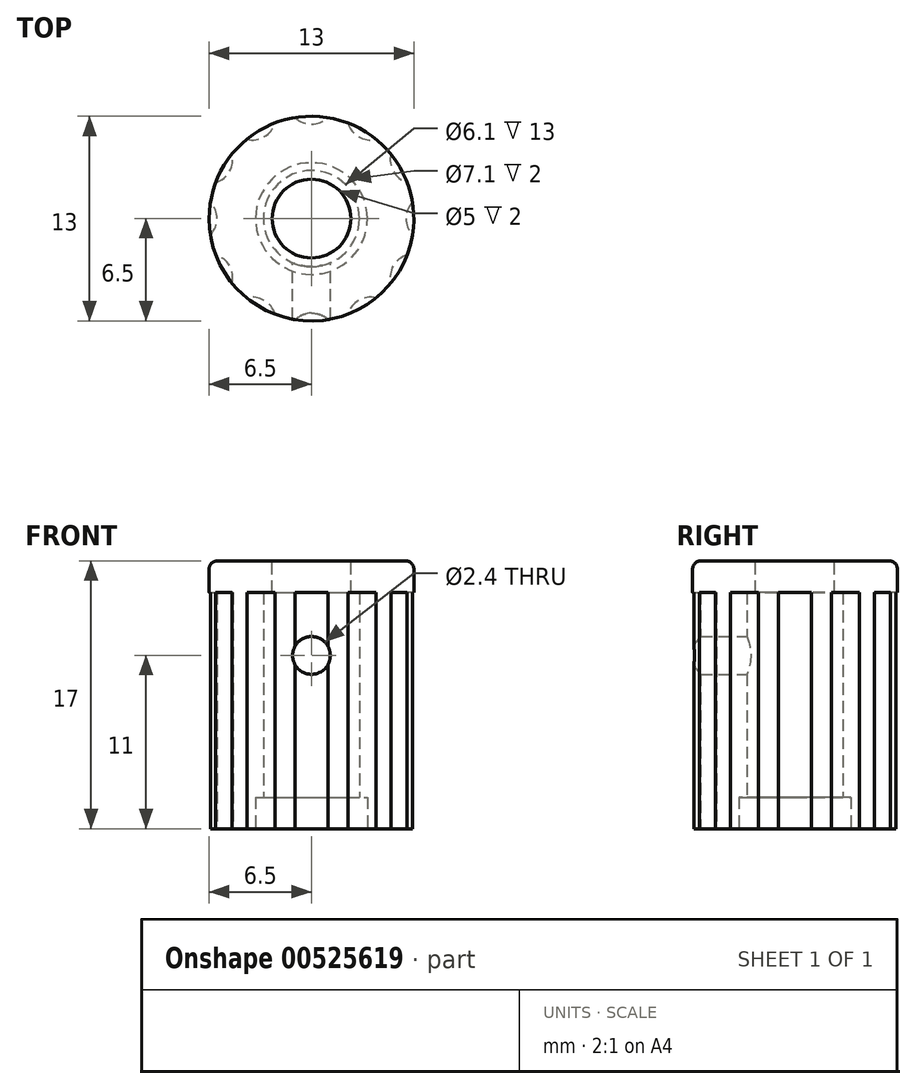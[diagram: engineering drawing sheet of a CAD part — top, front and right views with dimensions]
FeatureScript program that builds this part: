
annotation { "Feature Type Name" : "Feature", "Feature Type Description" : "" }
export const myFeature = defineFeature(function(context is Context, id is Id, definition is map)
    precondition{}
    {
        {
            var Q0;
            Q0=qCreatedBy(makeId("Front.planeOp"),FACE);
            var sketch = newSketch(context, id + "F0", { "sketchPlane" : qUnion([Q0])});
            skLineSegment(sketch, "E0", {"start": v(0, -2.23) * mm, "end": v(0, -5.1) * mm, "construction": true});
            skLineSegment(sketch, "E1", {"start": v(0, 0) * mm, "end": v(-5, 0) * mm});
            skLineSegment(sketch, "E2", {"start": v(-5, 0) * mm, "end": v(-5, 0) * mm});
            skLineSegment(sketch, "E3", {"start": v(-5, 0) * mm, "end": v(-6.5, 0) * mm});
            skLineSegment(sketch, "E4", {"start": v(-6.5, 0) * mm, "end": v(-6.5, 17) * mm});
            skLineSegment(sketch, "E5", {"start": v(-6.5, 17) * mm, "end": v(0, 17) * mm});
            skLineSegment(sketch, "E6", {"start": v(0, 0) * mm, "end": v(0, 17) * mm});
            skSolve(sketch);
        }
        {
            var Q0;
            Q0=qSketchRegion(id+"F0",true);
            var Q1;
            Q1=sQuery(id+"F0.wireOp",EDGE,"E0");
            revolve(context, id + "F1", {"entities" : qUnion([Q0]), "axis" : qUnion([Q1]), "revolveType" : RevolveType.FULL});
        }
        {
            var Q0;
            Q0=makeQuery(id+"F1.opRevolve","SWEPT_FACE",FACE,{"disambiguationData":[OSD([sQuery(id+"F0.wireOp",EDGE,"E1")])]});
            var sketch = newSketch(context, id + "F2", { "sketchPlane" : qUnion([Q0])});
            skCircle(sketch, "E7", {"center": v(0, 0) * mm, "radius": 3.05 * mm});
            skSolve(sketch);
        }
        {
            var Q0;
            Q0=qSketchRegion(id+"F2",true);
            extrude(context, id + "F3", {"entities" : qUnion([Q0]), "operationType" : NewBodyOperationType.REMOVE, "oppositeDirection" : true, "depth" : 15 * mm, "offsetDistance" : 25 * mm});
        }
        {
            var Q0;
            Q0=makeQuery(id+"F1.opRevolve","SWEPT_EDGE",EDGE,{"disambiguationData":[OSD([sQuery(id+"F0.wireOp",EDGE,"E4"),sQuery(id+"F0.wireOp",EDGE,"E5")])]});
            fillet(context, id + "F4", {"entities" : qUnion([Q0]), "radius" : 0.5 * mm, "tangentPropagation" : true, "allowEdgeOverflow" : false});
        }
        {
            var Q0;
            Q0=qCreatedBy(makeId("Front.planeOp"),FACE);
            var sketch = newSketch(context, id + "F5", { "sketchPlane" : qUnion([Q0])});
            skCircle(sketch, "E8", {"center": v(0, 11) * mm, "radius": 1.2 * mm});
            skSolve(sketch);
        }
        {
            var Q0;
            Q0=qSketchRegion(id+"F5",true);
            extrude(context, id + "F6", {"entities" : qUnion([Q0]), "operationType" : NewBodyOperationType.REMOVE, "depth" : 7 * mm, "offsetDistance" : 25 * mm});
        }
        {
            var Q0;
            Q0=makeQuery(id+"F1.opRevolve","SWEPT_FACE",FACE,{"disambiguationData":[OSD([sQuery(id+"F0.wireOp",EDGE,"E3")])]});
            var sketch = newSketch(context, id + "F7", { "sketchPlane" : qUnion([Q0])});
            skCircle(sketch, "E9", {"center": v(-7.5, 0) * mm, "radius": 1.5 * mm});
            skCircle(sketch, "E10.1.0", {"center": v(-6.5, -3.75) * mm, "radius": 1.5 * mm});
            skCircle(sketch, "E10.2.0", {"center": v(-3.75, -6.5) * mm, "radius": 1.5 * mm});
            skCircle(sketch, "E10.3.0", {"center": v(0, -7.5) * mm, "radius": 1.5 * mm});
            skCircle(sketch, "E10.4.0", {"center": v(3.75, -6.5) * mm, "radius": 1.5 * mm});
            skCircle(sketch, "E10.5.0", {"center": v(6.5, -3.75) * mm, "radius": 1.5 * mm});
            skCircle(sketch, "E10.6.0", {"center": v(7.5, 0) * mm, "radius": 1.5 * mm});
            skCircle(sketch, "E10.7.0", {"center": v(6.5, 3.75) * mm, "radius": 1.5 * mm});
            skCircle(sketch, "E10.8.0", {"center": v(3.75, 6.5) * mm, "radius": 1.5 * mm});
            skCircle(sketch, "E10.9.0", {"center": v(0, 7.5) * mm, "radius": 1.5 * mm});
            skCircle(sketch, "E10.10.0", {"center": v(-3.75, 6.5) * mm, "radius": 1.5 * mm});
            skCircle(sketch, "E10.11.0", {"center": v(-6.5, 3.75) * mm, "radius": 1.5 * mm});
            skPoint(sketch, "E10.center", {"position": v(0, 0) * mm});
            skSolve(sketch);
        }
        {
            var Q0;
            Q0=qSketchRegion(id+"F7",true);
            extrude(context, id + "F8", {"entities" : qUnion([Q0]), "operationType" : NewBodyOperationType.REMOVE, "oppositeDirection" : true, "depth" : 15 * mm, "offsetDistance" : 25 * mm});
        }
        {
            var Q0;
            Q0=makeQuery(id+"F1.opRevolve","SWEPT_FACE",FACE,{"disambiguationData":[OSD([sQuery(id+"F0.wireOp",EDGE,"E1")])]});
            var sketch = newSketch(context, id + "F9", { "sketchPlane" : qUnion([Q0])});
            skCircle(sketch, "E11", {"center": v(0, 0) * mm, "radius": 3.55 * mm});
            skSolve(sketch);
        }
        {
            var Q0;
            Q0=qSketchRegion(id+"F9",true);
            extrude(context, id + "F10", {"entities" : qUnion([Q0]), "operationType" : NewBodyOperationType.REMOVE, "oppositeDirection" : true, "depth" : 2 * mm, "offsetDistance" : 25 * mm});
        }
        {
            var Q0;
            Q0=makeQuery(id+"F1.opRevolve","SWEPT_FACE",FACE,{"disambiguationData":[OSD([sQuery(id+"F0.wireOp",EDGE,"E5")])]});
            var sketch = newSketch(context, id + "F11", { "sketchPlane" : qUnion([Q0])});
            skCircle(sketch, "E12", {"center": v(0, 0) * mm, "radius": 2.5 * mm});
            skSolve(sketch);
        }
        {
            var Q0;
            Q0 = qSketchRegion(id + "F11", true);
            extrude(context, id + "F12", {"entities" : qUnion([Q0]), "operationType" : NewBodyOperationType.REMOVE, "oppositeDirection" : true, "depth" : 3 * mm, "offsetDistance" : 25 * mm});
        }
    });
